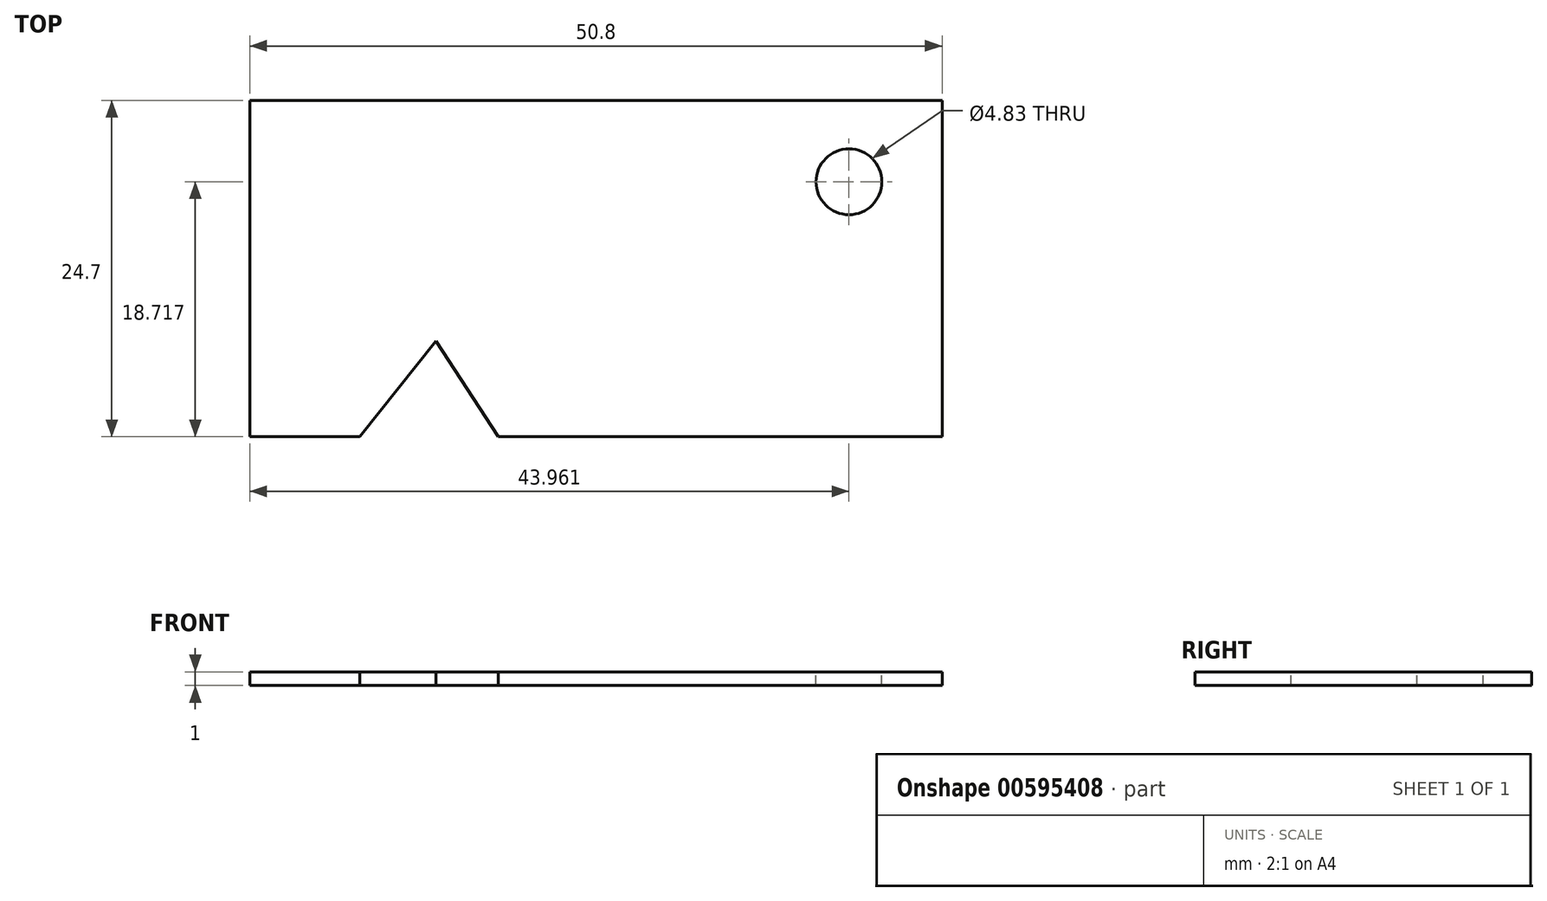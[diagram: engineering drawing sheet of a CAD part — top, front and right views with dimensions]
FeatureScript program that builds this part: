
annotation { "Feature Type Name" : "Feature", "Feature Type Description" : "" }
export const myFeature = defineFeature(function(context is Context, id is Id, definition is map)
    precondition{}
    {
        {
            var Q0;
            Q0=qCreatedBy(makeId("Top.planeOp"),FACE);
            var sketch = newSketch(context, id + "F0", { "sketchPlane" : qUnion([Q0])});
            skLineSegment(sketch, "E0.bottom", {"start": v(-25.4, 12.35) * mm, "end": v(25.4, 12.35) * mm});
            skLineSegment(sketch, "E0.top", {"start": v(-25.4, -12.35) * mm, "end": v(25.4, -12.35) * mm});
            skLineSegment(sketch, "E0.left", {"start": v(-25.4, 12.35) * mm, "end": v(-25.4, -12.35) * mm});
            skLineSegment(sketch, "E0.right", {"start": v(25.4, 12.35) * mm, "end": v(25.4, -12.35) * mm});
            skPoint(sketch, "E0.middle", {"position": v(0, 0) * mm});
            skSolve(sketch);
        }
        {
            var Q0;
            Q0 = qSketchRegion(id + "F0", true);
            extrude(context, id + "F1", {"entities" : qUnion([Q0]), "depth" : 1 * mm, "offsetDistance" : 25 * mm});
        }
        {
            var Q0;
            Q0=makeQuery(id+"F1.opExtrude","CAP_FACE",FACE,{"disambiguationData":[OSD([sQuery(id+"F0.wireOp",EDGE,"E0.bottom"),sQuery(id+"F0.wireOp",EDGE,"E0.top"),sQuery(id+"F0.wireOp",EDGE,"E0.left"),sQuery(id+"F0.wireOp",EDGE,"E0.right")])],"isStart":false});
            var sketch = newSketch(context, id + "F2", { "sketchPlane" : qUnion([Q0])});
            skCircle(sketch, "E1", {"center": v(19.32, -3.54) * mm, "radius": 1.5 * mm});
            skSolve(sketch);
        }
        {
            var Q0;
            Q0 = qSketchRegion(id + "F2", true);
            extrude(context, id + "F3", {"entities" : qUnion([Q0]), "operationType" : NewBodyOperationType.REMOVE, "depth" : 33.2 * mm, "offsetDistance" : 25 * mm});
        }
        {
            var Q0;
            Q0=makeQuery(id+"F1.opExtrude","CAP_FACE",FACE,{"disambiguationData":[OSD([sQuery(id+"F0.wireOp",EDGE,"E0.bottom"),sQuery(id+"F0.wireOp",EDGE,"E0.top"),sQuery(id+"F0.wireOp",EDGE,"E0.left"),sQuery(id+"F0.wireOp",EDGE,"E0.right")])],"isStart":false});
            var sketch = newSketch(context, id + "F4", { "sketchPlane" : qUnion([Q0])});
            skCircle(sketch, "E2", {"center": v(18.56, 6.37) * mm, "radius": 2.41 * mm});
            skSolve(sketch);
        }
        {
            var Q0;
            Q0 = qSketchRegion(id + "F4", true);
            extrude(context, id + "F5", {"entities" : qUnion([Q0]), "operationType" : NewBodyOperationType.REMOVE, "oppositeDirection" : true, "depth" : 25 * mm, "offsetDistance" : 25 * mm});
        }
        {
            var Q0;
            Q0=makeQuery(id+"F1.opExtrude","CAP_FACE",FACE,{"disambiguationData":[OSD([sQuery(id+"F0.wireOp",EDGE,"E0.bottom"),sQuery(id+"F0.wireOp",EDGE,"E0.top"),sQuery(id+"F0.wireOp",EDGE,"E0.left"),sQuery(id+"F0.wireOp",EDGE,"E0.right")])],"isStart":false});
            var sketch = newSketch(context, id + "F6", { "sketchPlane" : qUnion([Q0])});
            skLineSegment(sketch, "E3", {"start": v(-17.33, -12.35) * mm, "end": v(-11.34, -4.8) * mm});
            skLineSegment(sketch, "E4", {"start": v(-12.06, -4.8) * mm, "end": v(-7.17, -12.35) * mm});
            skSolve(sketch);
        }
        {
            var Q0;
            {var subQ0=sQuery(id+"F6.wireOp",EDGE,"E3");var subQ1=makeQuery(id+"F1.opExtrude","CAP_EDGE",EDGE,{"disambiguationData":[OSD([sQuery(id+"F0.wireOp",EDGE,"E0.top")])],"isStart":false});var subQ2=makeQuery(id+"F6.imprint","INTERSECT",VERTEX,{"derivedFrom":[subQ1,subQ0]});Q0=makeQuery(id+"F6.imprint","IMPRINT",FACE,{"disambiguationData":[TD([[makeQuery(id+"F6.imprint","IMPRINT",EDGE,{"disambiguationData":[TD([[subQ2,-1.0]])],"derivedFrom":subQ0}),-1.0]])]});}
            extrude(context, id + "F7", {"entities" : qUnion([Q0]), "operationType" : NewBodyOperationType.REMOVE, "oppositeDirection" : true, "depth" : 25 * mm, "offsetDistance" : 25 * mm});
        }
    });
